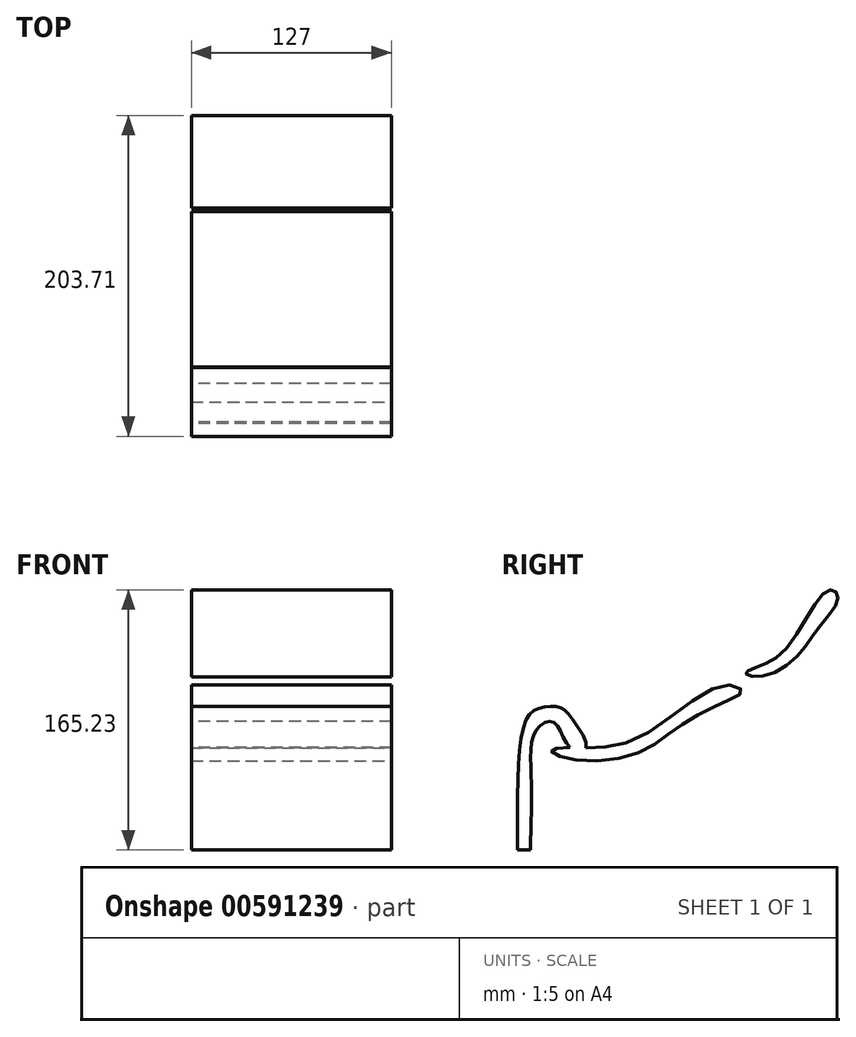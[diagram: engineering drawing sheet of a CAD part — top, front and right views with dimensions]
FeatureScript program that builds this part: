
annotation { "Feature Type Name" : "Feature", "Feature Type Description" : "" }
export const myFeature = defineFeature(function(context is Context, id is Id, definition is map)
    precondition{}
    {
        {
            var Q0;
            Q0=qCreatedBy(makeId("Right.planeOp"),FACE);
            var sketch = newSketch(context, id + "F0", { "sketchPlane" : qUnion([Q0])});
            skFitSpline(sketch, "E0", {"points": [v(-117.89, -39.26) * mm, v(-76.76, -34.1) * mm, v(-21.38, 0) * mm, v(-8.79, -3.43) * mm, v(-18.49, -9.8) * mm, v(-47.86, -25.34) * mm, v(-75.4, -43) * mm, v(-119.6, -46.3) * mm, v(-129.76, -41.24) * mm, v(-117.89, -39.26) * mm]});
            skFitSpline(sketch, "E1", {"points": [v(0, 11.5) * mm, v(19.5, 23.78) * mm, v(43.07, 58.65) * mm, v(50.44, 60.13) * mm, v(51.92, 53.74) * mm, v(40.13, 37.04) * mm, v(22.93, 15.43) * mm, v(0, 5.6) * mm, v(-6.54, 8.06) * mm, v(0, 11.5) * mm]});
            skFitSpline(sketch, "E2", {"points": [v(-143.24, -104.35) * mm, v(-142.7, -58.16) * mm, v(-139.44, -28.27) * mm, v(-128.02, -23.38) * mm, v(-117.89, -39.26) * mm, v(-107.86, -39.44) * mm, v(-117.89, -19.57) * mm, v(-125.3, -13.6) * mm, v(-137.26, -14.14) * mm, v(-146.5, -23.38) * mm, v(-151.4, -104.35) * mm], "startDerivative": vector(10.09, 327.8) * mm, "endDerivative": vector(3.49, -527.4) * mm});
            skFitSpline(sketch, "E3", {"points": [v(-151.4, -104.35) * mm, v(-143.24, -104.35) * mm], "startDerivative": vector(8.15, 0) * mm, "endDerivative": vector(8.15, 0) * mm});
            skSolve(sketch);
        }
        {
            var Q0;
            Q0=makeQuery(id+"F0.imprint","IMPRINT",FACE,{"disambiguationData":[TD([[makeQuery(id+"F0.imprint","IMPRINT",EDGE,{"derivedFrom":sQuery(id+"F0.wireOp",EDGE,"E1")}),-1.0]])]});
            var Q1;
            {var subQ0=sQuery(id+"F0.wireOp",EDGE,"E2");var subQ1=sQuery(id+"F0.wireOp",EDGE,"E0");var subQ2=makeQuery(id+"F0.imprint","INTERSECT",VERTEX,{"disambiguationData":[OD(0.0)],"derivedFrom":[subQ1,subQ0]});Q1=makeQuery(id+"F0.imprint","IMPRINT",FACE,{"disambiguationData":[TD([[makeQuery(id+"F0.imprint","IMPRINT",EDGE,{"disambiguationData":[TD([[subQ2,-1.0]])],"derivedFrom":subQ1}),-1.0]])]});}
            var Q2;
            {var subQ4=sQuery(id+"F0.wireOp",EDGE,"E3");Q2=makeQuery(id+"F0.imprint","IMPRINT",FACE,{"disambiguationData":[TD([[makeQuery(id+"F0.imprint","IMPRINT",EDGE,{"derivedFrom":subQ4}),1.0]])]});}
            var Q3;
            {var subQ0=sQuery(id+"F0.wireOp",EDGE,"E2");var subQ1=sQuery(id+"F0.wireOp",EDGE,"E0");var subQ2=makeQuery(id+"F0.imprint","INTERSECT",VERTEX,{"disambiguationData":[OD(0.0)],"derivedFrom":[subQ1,subQ0]});Q3=makeQuery(id+"F0.imprint","IMPRINT",FACE,{"disambiguationData":[TD([[makeQuery(id+"F0.imprint","IMPRINT",EDGE,{"disambiguationData":[TD([[subQ2,1.0]])],"derivedFrom":subQ1}),-1.0]])]});}
            extrude(context, id + "F1", {"entities" : qUnion([Q0, Q1, Q2, Q3]), "endBound" : BoundingType.SYMMETRIC, "depth" : 127 * mm, "offsetDistance" : 25.4 * mm});
        }
    });
